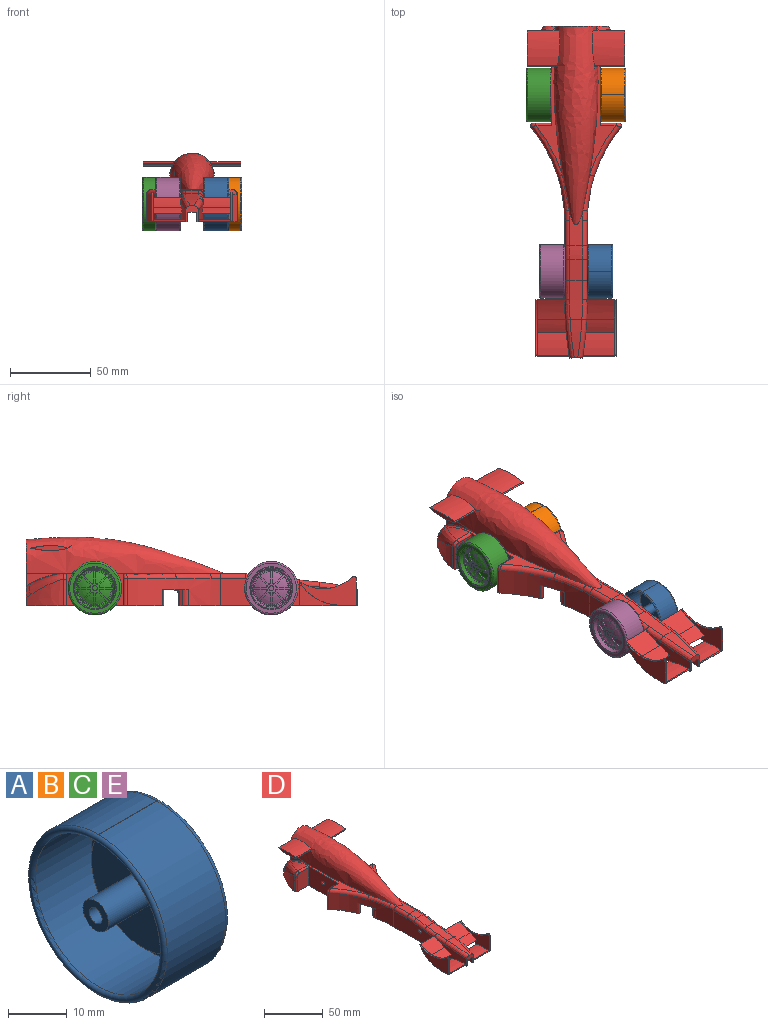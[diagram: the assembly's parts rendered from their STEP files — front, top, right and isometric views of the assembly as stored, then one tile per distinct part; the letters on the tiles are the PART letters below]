
ASSEMBLY  parts=5 mates=4
PART A: 90 faces, bbox 16.1x36.1x36.1 mm
  f0: cylinder r=16.5mm len=16.5mm, axis (1,0,0), area 362.7mm2, adj f1,f3,f86,f88
  f1: torus R=15.5mm, axis (1,0,0), area 159.3mm2, adj f0,f2,f7,f84,f85,f86,f87,f88
  f2: cylinder r=16.5mm len=33mm, axis (1,0,0), area 1088.4mm2, adj f1,f3,f84,f87
  f3: torus R=15.81mm, axis (1,0,0), area 215.3mm2, adj f0,f2,f8,f84,f85,f86,f87,f88
  f4: torus R=13.24mm, axis (1,0,0), area 10.3mm2, adj f7,f15
  f5: cylinder r=1.55mm len=13mm, axis (1,0,0), area 126.6mm2, adj f6,f13
  f6: cone r=1.55mm half-angle=51.1deg, axis (-1,0,0), area 9.7mm2, adj f5
  f7: plane 31x31mm, normal (1,0,0), area 203.7mm2, adj f1,f4
  f8: cylinder r=15.12mm len=30.24mm, axis (1,0,0), area 1282.5mm2, adj f3,f9
  f9: plane 30.24x30.24mm, normal (-1,0,0), area 177.4mm2, adj f8,f10
  f10: cone r=13.12mm half-angle=16.7deg, axis (1,0,0), area 249.3mm2, adj f9,f11
  f11: plane 24.44x24.44mm, normal (-1,0,0), area 439.9mm2, adj f10,f12
  f12: cylinder r=3.05mm len=11.19mm, axis (1,0,0), area 214.4mm2, adj f11,f13
  f13: plane 6.1x6.1mm, normal (-1,0,0), area 21.7mm2, adj f5,f12
  f14: plane 26.24x26.24mm, normal (1,0,0), area 49.9mm2, adj f15,f17
  f15: cylinder r=13.12mm len=26.24mm, axis (1,0,0), area 0.6mm2, adj f4,f14
  f16: plane 3x3mm, normal (1,0,0), area 7.1mm2, adj f61
  f17: cone r=12.5mm half-angle=16.7deg, axis (1,0,0), area 188.9mm2, adj f14,f18
  f18: torus R=11.31mm, axis (1,0,0), area 65.6mm2, adj f17,f24,f30,f36,f42,f48,f54,f60
  f19: cylinder r=0.75mm len=1.28mm, axis (1,0,0), area 1.3mm2, adj f20,f23,f61,f68
  f20: plane 7.03x3.12mm, normal (0,-1,0), area 4.9mm2, adj f19,f21,f61,f68
  f21: cylinder r=1mm len=1.16mm, axis (1,0,0), area 1.1mm2, adj f20,f24,f61,f68,f69
  f22: cylinder r=1mm len=1.52mm, axis (1,0,0), area 1.1mm2, adj f23,f24,f61,f68,f69
  f23: plane 5.1x5.1mm, normal (0,0.71,-0.71), area 4.9mm2, adj f19,f22,f61,f68
  f24: cylinder r=11.05mm len=4.66mm, axis (1,0,0), area 1.8mm2, adj f18,f21,f22,f69
  f25: cylinder r=1mm len=1.16mm, axis (1,0,0), area 1.1mm2, adj f26,f30,f61,f70,f71
  f26: plane 7.03x3.12mm, normal (0,0,-1), area 4.9mm2, adj f25,f27,f61,f71
  f27: cylinder r=0.75mm len=1.28mm, axis (1,0,0), area 1.3mm2, adj f26,f29,f61,f71
  f28: cylinder r=1mm len=1.52mm, axis (1,0,0), area 1.1mm2, adj f29,f30,f61,f70,f71
  f29: plane 5.1x5.1mm, normal (0,-0.71,0.71), area 4.9mm2, adj f27,f28,f61,f71
  f30: cylinder r=11.05mm len=4.66mm, axis (1,0,0), area 1.8mm2, adj f18,f25,f28,f70
  f31: plane 7.03x3.12mm, normal (0,0,1), area 4.9mm2, adj f32,f35,f61,f72
  f32: cylinder r=1mm len=1.16mm, axis (1,0,0), area 1.1mm2, adj f31,f36,f61,f72,f73
  f33: cylinder r=1mm len=1.52mm, axis (1,0,0), area 1.1mm2, adj f34,f36,f61,f72,f73
  f34: plane 5.1x5.1mm, normal (0,-0.71,-0.71), area 4.9mm2, adj f33,f35,f61,f72
  f35: cylinder r=0.75mm len=1.28mm, axis (1,0,0), area 1.3mm2, adj f31,f34,f61,f72
  f36: cylinder r=11.05mm len=4.66mm, axis (1,0,0), area 1.8mm2, adj f18,f32,f33,f73
  f37: plane 5.1x5.1mm, normal (0,0.71,0.71), area 4.9mm2, adj f38,f41,f61,f80
  f38: cylinder r=1mm len=1.52mm, axis (1,0,0), area 1.1mm2, adj f37,f42,f61,f80,f81
  f39: cylinder r=1mm len=1.16mm, axis (1,0,0), area 1.1mm2, adj f40,f42,f61,f80,f81
  f40: plane 7.03x3.12mm, normal (0,-1,0), area 4.9mm2, adj f39,f41,f61,f80
  f41: cylinder r=0.75mm len=1.28mm, axis (1,0,0), area 1.3mm2, adj f37,f40,f61,f80
  f42: cylinder r=11.05mm len=4.66mm, axis (1,0,0), area 1.8mm2, adj f18,f38,f39,f81
  f43: plane 7.03x3.12mm, normal (0,1,0), area 4.9mm2, adj f44,f47,f61,f74
  f44: cylinder r=1mm len=1.16mm, axis (1,0,0), area 1.1mm2, adj f43,f48,f61,f74,f75
  f45: cylinder r=1mm len=1.52mm, axis (1,0,0), area 1.1mm2, adj f46,f48,f61,f74,f75
  f46: plane 5.1x5.1mm, normal (0,-0.71,0.71), area 4.9mm2, adj f45,f47,f61,f74
  f47: cylinder r=0.75mm len=1.28mm, axis (1,0,0), area 1.3mm2, adj f43,f46,f61,f74
  f48: cylinder r=11.05mm len=4.66mm, axis (1,0,0), area 1.8mm2, adj f18,f44,f45,f75
  f49: plane 5.1x5.1mm, normal (0,0.71,-0.71), area 4.9mm2, adj f50,f53,f61,f76
  f50: cylinder r=1mm len=1.52mm, axis (1,0,0), area 1.1mm2, adj f49,f54,f61,f76,f77
  f51: cylinder r=1mm len=1.16mm, axis (1,0,0), area 1.1mm2, adj f52,f54,f61,f76,f77
  f52: plane 7.03x3.12mm, normal (0,0,1), area 4.9mm2, adj f51,f53,f61,f76
  f53: cylinder r=0.75mm len=1.28mm, axis (1,0,0), area 1.3mm2, adj f49,f52,f61,f76
  f54: cylinder r=11.05mm len=4.66mm, axis (1,0,0), area 1.8mm2, adj f18,f50,f51,f77
  f55: plane 7.03x3.12mm, normal (0,0,-1), area 4.9mm2, adj f56,f59,f61,f78
  f56: cylinder r=1mm len=1.16mm, axis (1,0,0), area 1.1mm2, adj f55,f60,f61,f78,f79
  f57: cylinder r=1mm len=1.52mm, axis (1,0,0), area 1.1mm2, adj f58,f60,f61,f78,f79
  f58: plane 5.1x5.1mm, normal (0,0.71,0.71), area 4.9mm2, adj f57,f59,f61,f78
  f59: cylinder r=0.75mm len=1.28mm, axis (1,0,0), area 1.3mm2, adj f55,f58,f61,f78
  f60: cylinder r=11.05mm len=4.66mm, axis (1,0,0), area 1.8mm2, adj f18,f56,f57,f79
  f61: torus R=1.5mm, axis (1,0,0), area 131.6mm2, adj f16,f18,f19,f20,f21,f22,f23,f25
  f62: plane 5.1x5.1mm, normal (0,-0.71,-0.71), area 4.9mm2, adj f61,f63,f66,f82
  f63: cylinder r=1mm len=1.52mm, axis (1,0,0), area 1.1mm2, adj f61,f62,f67,f82,f83
  f64: cylinder r=1mm len=1.16mm, axis (1,0,0), area 1.1mm2, adj f61,f65,f67,f82,f83
  f65: plane 7.03x3.12mm, normal (0,1,0), area 4.9mm2, adj f61,f64,f66,f82
  f66: cylinder r=0.75mm len=1.28mm, axis (1,0,0), area 1.3mm2, adj f61,f62,f65,f82
  f67: cylinder r=11.05mm len=4.66mm, axis (1,0,0), area 1.8mm2, adj f18,f63,f64,f83
  f68: torus R=1.5mm, axis (1,0,0), area 29.3mm2, adj f19,f20,f21,f22,f23,f69
  f69: plane 6.16x3.12mm, normal (1,0,0), area 4.5mm2, adj f21,f22,f24,f68
  f70: plane 6.16x3.12mm, normal (1,0,0), area 4.5mm2, adj f25,f28,f30,f71
  f71: torus R=1.5mm, axis (1,0,0), area 29.3mm2, adj f25,f26,f27,f28,f29,f70
  f72: torus R=1.5mm, axis (1,0,0), area 29.3mm2, adj f31,f32,f33,f34,f35,f73
  f73: plane 6.16x3.12mm, normal (1,0,0), area 4.5mm2, adj f32,f33,f36,f72
  f74: torus R=1.5mm, axis (1,0,0), area 29.3mm2, adj f43,f44,f45,f46,f47,f75
  f75: plane 6.16x3.12mm, normal (1,0,0), area 4.5mm2, adj f44,f45,f48,f74
  f76: torus R=1.5mm, axis (1,0,0), area 29.3mm2, adj f49,f50,f51,f52,f53,f77
  f77: plane 6.16x3.12mm, normal (1,0,0), area 4.5mm2, adj f50,f51,f54,f76
  f78: torus R=1.5mm, axis (1,0,0), area 29.3mm2, adj f55,f56,f57,f58,f59,f79
  f79: plane 6.16x3.12mm, normal (1,0,0), area 4.5mm2, adj f56,f57,f60,f78
  f80: torus R=1.5mm, axis (1,0,0), area 29.3mm2, adj f37,f38,f39,f40,f41,f81
  f81: plane 6.16x3.12mm, normal (1,0,0), area 4.5mm2, adj f38,f39,f42,f80
  f82: torus R=1.5mm, axis (1,0,0), area 29.3mm2, adj f62,f63,f64,f65,f66,f83
  f83: plane 6.16x3.12mm, normal (1,0,0), area 4.5mm2, adj f63,f64,f67,f82
  f84: plane 14.18x0.01mm, normal (0,1,0), area 0.1mm2, adj f1,f2,f3,f85
  f85: plane 14.18x0.01mm, normal (0,0,1), area 0.1mm2, adj f1,f3,f84,f86
  f86: plane 14.18x0.01mm, normal (0,-1,0), area 0.1mm2, adj f0,f1,f3,f85
  f87: plane 14.18x0.01mm, normal (0,0,1), area 0.1mm2, adj f1,f2,f3,f89
  f88: plane 14.18x0.01mm, normal (0,0,-1), area 0.1mm2, adj f0,f1,f3,f89
  f89: plane 14.18x0.01mm, normal (0,1,0), area 0.1mm2, adj f1,f3,f87,f88
PART B: same geometry as A
PART C: same geometry as A
PART D: 160 faces, bbox 60.7x214.2x51 mm
  f0: plane 66.79x20.53mm, normal (0,0,1), area 391.4mm2, adj f3,f6,f43,f49,f107,f116,f120,f143
  f1: plane 66.78x20.53mm, normal (0,0,1), area 391.4mm2, adj f2,f5,f6,f42,f47,f116,f129,f140
  f2: bspline ~135x17.28mm, area 183.9mm2, adj f1,f5,f6,f116
  f3: bspline ~135x17.28mm, area 183.9mm2, adj f0,f6,f107,f116
  f4: plane 21.67x8.38mm, normal (0,0,1), area 126mm2, adj f6,f22,f122,f123,f131,f132
  f5: plane 9.31x0.16mm, normal (0,-1,0), area 1.5mm2, adj f1,f2,f106,f116
  f6: bspline ~122.68x27.34mm, area 5446.4mm2, adj f0,f1,f2,f3,f4,f7,f105,f106
  f7: plane 41.59x40.59mm, normal (0,1,0), area 629.2mm2, adj f6,f32,f36,f41,f45,f50,f55,f57
  f8: extruded ~24.99x7.5mm, area 9.7mm2, adj f49,f55,f105
  f9: extruded ~24.99x7.5mm, area 11.3mm2, adj f47,f57,f106
  f10: cylinder r=53.29mm len=20.77mm, axis (-1,0,0), area 290.9mm2, adj f11,f12,f17,f96,f98
  f11: cylinder r=53.29mm len=19.77mm, axis (-1,0,0), area 276.2mm2, adj f10,f12,f17,f99
  f12: cylinder r=0.45mm len=20.77mm, axis (-1,0,0), area 26.6mm2, adj f10,f11,f17,f97,f98,f99
  f13: cylinder r=62.23mm len=17.75mm, axis (-1,0,0), area 232.9mm2, adj f14,f16,f17,f99,f136
  f14: cylinder r=50mm len=17.93mm, axis (-1,0,0), area 157mm2, adj f13,f15,f17,f99
  f15: plane 17.93x2.95mm, normal (0,0.17,-0.98), area 53.4mm2, adj f14,f16,f17,f99
  f16: cylinder r=29.92mm len=17.75mm, axis (-1,0,0), area 344.5mm2, adj f13,f15,f17,f99,f136
  f17: cylinder r=220.68mm len=36.26mm, axis (0,0,1), area 336.4mm2, adj f10,f11,f12,f13,f14,f15,f16,f27
  f18: cylinder r=220.68mm len=36.26mm, axis (0,0,1), area 336.4mm2, adj f20,f27,f86,f88,f89,f90,f91,f92
  f19: plane 72.73x29.07mm, normal (0,0,-1), area 836.9mm2, adj f25,f26,f32,f34,f35,f61,f69,f70
  f20: plane 110.7x6.33mm, normal (0,0,-1), area 239.3mm2, adj f18,f25,f27,f28,f82,f85,f86,f148
  f21: plane 12.97x8mm, normal (0,-0.14,0.99), area 104.8mm2, adj f22,f24,f125,f134
  f22: cylinder r=60mm len=8.49mm, axis (1,0,0), area 68.1mm2, adj f4,f21,f124,f133
  f23: bspline ~30x30mm, area 118.3mm2, adj f24,f27,f128,f137
  f24: bspline ~24.13x11.17mm, area 190.1mm2, adj f21,f23,f126,f127,f135,f136
  f25: plane 10x6.68mm, normal (0.87,0.48,0), area 20.6mm2, adj f19,f20,f76,f146,f147,f148,f158
  f26: cylinder r=30mm len=10mm, axis (0,0,-1), area 84.3mm2, adj f19,f41,f69,f144
  f27: plane 10.49x8.49mm, normal (0,-1,0), area 40.4mm2, adj f17,f18,f20,f23,f44,f82,f128,f137
  f28: plane 69.2x7.24mm, normal (-1,0,0), area 466.2mm2, adj f20,f34,f38,f64,f82,f148
  f29: plane 69.2x7.25mm, normal (1,0,0), area 466.2mm2, adj f35,f39,f44,f65,f82,f149
  f30: plane 21x1.69mm, normal (0,0,-1), area 35.4mm2, adj f31,f33,f37,f71
  f31: plane 5.87x2.1mm, normal (-1,0,0), area 8mm2, adj f30,f37,f40,f71
  f32: plane 75.59x10mm, normal (1,0,0), area 697.4mm2, adj f7,f19,f36,f59,f72,f73,f74,f75
  f33: plane 5.87x2.1mm, normal (1,0,0), area 8mm2, adj f30,f37,f40,f71
  f34: extruded ~48.21x2.99mm, area 170.3mm2, adj f19,f28,f62,f80,f81,f147
  f35: extruded ~48.21x2.99mm, area 170.3mm2, adj f19,f29,f63,f78,f79,f150
  f36: plane 85.05x19.56mm, normal (0,0,-1), area 808mm2, adj f7,f32,f42,f45,f48,f54,f73,f83
  f37: cylinder r=1.6mm len=30mm, axis (-1,0,0), area 241.4mm2, adj f30,f31,f33,f40,f42,f43
  f38: extruded ~0.48x0.41mm, area 0.1mm2, adj f28,f66,f82
  f39: extruded ~0.48x0.41mm, area 0.1mm2, adj f29,f67,f82
  f40: plane 21x1.69mm, normal (0,0,-1), area 35.4mm2, adj f31,f33,f37,f71
  f41: plane 85.05x19.56mm, normal (0,0,-1), area 808mm2, adj f7,f26,f43,f50,f52,f53,f69,f85
  f42: plane 38.14x20.05mm, normal (-1,0,0), area 693mm2, adj f1,f36,f37,f47,f48,f54,f140,f153
  f43: plane 38.14x20.05mm, normal (1,0,0), area 693mm2, adj f0,f37,f41,f49,f52,f53,f143,f155
  f44: plane 110.7x6.33mm, normal (0,0,-1), area 238.4mm2, adj f17,f27,f29,f70,f82,f83,f84,f149
  f45: bspline ~25x20mm, area 284mm2, adj f7,f36,f57,f58,f152
  f46: bspline ~25x15mm, area 104.7mm2, adj f47,f58,f153
  f47: extruded ~24.39x7.22mm, area 46.3mm2, adj f1,f9,f42,f46,f57
  f48: plane 18.46x13.45mm, normal (0,-1,0), area 247.4mm2, adj f36,f42,f152,f153,f154
  f49: extruded ~24.4x7.23mm, area 46.4mm2, adj f0,f8,f43,f51,f55
  f50: bspline ~25x20mm, area 284mm2, adj f7,f41,f55,f56,f156
  f51: bspline ~25x15mm, area 104.7mm2, adj f49,f56,f155
  f52: plane 18.46x13.44mm, normal (0,-1,0), area 247.4mm2, adj f41,f43,f155,f156,f157
  f53: plane 18.5x11.72mm, normal (0,1,0), area 216.1mm2, adj f41,f43,f141,f142,f143
  f54: plane 18.5x11.72mm, normal (0,1,0), area 216.1mm2, adj f36,f42,f138,f139,f140
  f55: bspline ~9.3x9.24mm, area 37.1mm2, adj f7,f8,f49,f50,f56
  f56: bspline ~27.26x18.15mm, area 196.7mm2, adj f50,f51,f55,f157
  f57: bspline ~9.3x9.24mm, area 37mm2, adj f7,f9,f45,f47,f58
  f58: bspline ~27.26x18.15mm, area 196.7mm2, adj f45,f46,f57,f154
  f59: plane 21.44x21mm, normal (0,0,-1), area 450.3mm2, adj f7,f32,f69,f74
  f60: cylinder r=41.85mm len=29.2mm, axis (-1,0,0), area 174.6mm2, adj f61,f62,f63,f64,f65,f66,f67,f68
  f61: cylinder r=2mm len=4.02mm, axis (-1,0,0), area 2.9mm2, adj f19,f60,f62,f63
  f62: bspline ~3.98x2.89mm, area 6.3mm2, adj f34,f60,f61,f64
  f63: bspline ~3.98x2.9mm, area 6.3mm2, adj f35,f60,f61,f65
  f64: torus R=43.85mm, axis (1,0,0), area 81.1mm2, adj f28,f60,f62,f66
  f65: torus R=43.85mm, axis (-1,0,0), area 81.1mm2, adj f29,f60,f63,f67
  f66: bspline ~3.98x2.89mm, area 5.8mm2, adj f38,f60,f64,f68,f82
  f67: bspline ~3.98x2.9mm, area 5.8mm2, adj f39,f60,f65,f68,f82
  f68: cylinder r=2mm len=4.02mm, axis (-1,0,0), area 2.1mm2, adj f60,f66,f67,f82
  f69: plane 75.59x10mm, normal (-1,0,0), area 697.4mm2, adj f7,f19,f26,f41,f59,f72,f74,f75
  f70: plane 10x6.68mm, normal (-0.87,0.48,0), area 20.6mm2, adj f19,f44,f77,f149,f150,f151,f159
  f71: cylinder r=3.1mm len=21mm, axis (-1,0,0), area 161.8mm2, adj f30,f31,f33,f40
  f72: cylinder r=41.85mm len=21.53mm, axis (-1,0,0), area 457.4mm2, adj f32,f69,f74,f75
  f73: cylinder r=30mm len=10mm, axis (0,0,-1), area 84.3mm2, adj f19,f32,f36,f145
  f74: cylinder r=40mm len=21mm, axis (-1,0,0), area 218.6mm2, adj f32,f59,f69,f72
  f75: cylinder r=40mm len=21mm, axis (-1,0,0), area 218.6mm2, adj f19,f32,f69,f72
  f76: plane 4.81x4.68mm, normal (0,0.08,-1), area 9.1mm2, adj f19,f25,f81,f146
  f77: plane 4.81x4.68mm, normal (0,0.08,-1), area 9.1mm2, adj f19,f70,f78,f151
  f78: bspline ~27.44x5.62mm, area 18.2mm2, adj f19,f35,f77,f79,f151
  f79: bspline ~25.87x5.18mm, area 12mm2, adj f35,f78,f151
  f80: bspline ~24.87x5.11mm, area 12mm2, adj f34,f81,f146
  f81: bspline ~32.15x6.03mm, area 18.2mm2, adj f19,f34,f76,f80,f146
  f82: bspline ~40x10mm, area 943.8mm2, adj f20,f27,f28,f29,f38,f39,f44,f66
  f83: cylinder r=89.76mm len=57.54mm, axis (0,0,1), area 891.9mm2, adj f19,f36,f44,f84,f129,f130,f131,f138
  f84: plane 48.74x17mm, normal (-1,0,0), area 760.8mm2, adj f17,f44,f83,f87,f132,f133,f134,f135
  f85: cylinder r=89.76mm len=57.54mm, axis (0,0,1), area 891.9mm2, adj f19,f20,f41,f86,f120,f121,f122,f141
  f86: plane 48.74x17mm, normal (1,0,0), area 760.8mm2, adj f18,f20,f85,f87,f123,f124,f125,f126
  f87: cylinder r=1.6mm len=14mm, axis (-1,0,0), area 140.7mm2, adj f84,f86
  f88: cylinder r=53.29mm len=19.77mm, axis (1,0,0), area 276.2mm2, adj f18,f89,f90,f100
  f89: cylinder r=53.29mm len=20.77mm, axis (1,0,0), area 290.9mm2, adj f18,f88,f90,f101,f104
  f90: cylinder r=0.45mm len=20.77mm, axis (1,0,0), area 26.6mm2, adj f18,f88,f89,f100,f103,f104
  f91: cylinder r=29.92mm len=17.75mm, axis (1,0,0), area 344.5mm2, adj f18,f92,f94,f100,f127
  f92: plane 17.93x2.95mm, normal (0,0.17,-0.98), area 53.4mm2, adj f18,f91,f93,f100
  f93: cylinder r=50mm len=17.93mm, axis (1,0,0), area 157mm2, adj f18,f92,f94,f100
  f94: cylinder r=62.23mm len=17.75mm, axis (1,0,0), area 232.9mm2, adj f18,f91,f93,f100,f127
  f95: cylinder r=26.41mm len=32.48mm, axis (1,0,0), area 35.1mm2, adj f96,f98,f99,f119
  f96: cylinder r=28.53mm len=20mm, axis (1,0,0), area 25.2mm2, adj f10,f95,f98,f99
  f97: plane 15.69x1mm, normal (0,-1,0), area 15.7mm2, adj f12,f98,f99,f119
  f98: plane 35x17.94mm, normal (-1,0,0), area 330.6mm2, adj f10,f12,f95,f96,f97,f119
  f99: plane 35x17.19mm, normal (1,0,0), area 286.5mm2, adj f11,f12,f13,f14,f15,f16,f95,f96
  f100: plane 35x17.19mm, normal (-1,0,0), area 286.5mm2, adj f88,f90,f91,f92,f93,f94,f101,f102
  f101: cylinder r=28.53mm len=20mm, axis (-1,0,0), area 25.2mm2, adj f89,f100,f102,f104
  f102: cylinder r=26.41mm len=32.48mm, axis (-1,0,0), area 35.1mm2, adj f100,f101,f104,f118
  f103: plane 15.69x1mm, normal (0,-1,0), area 15.7mm2, adj f90,f100,f104,f118
  f104: plane 35x17.94mm, normal (1,0,0), area 330.6mm2, adj f89,f90,f101,f102,f103,f118
  f105: extruded ~25x7.66mm, area 62.8mm2, adj f6,f7,f8,f107
  f106: extruded ~25x7.66mm, area 62.8mm2, adj f5,f6,f7,f9
  f107: plane 9.31x0.16mm, normal (0,-1,0), area 1.5mm2, adj f0,f3,f105,f116
  f108: plane 22x3mm, normal (-1,0,0), area 46.8mm2, adj f109,f110,f111
  f109: cylinder r=47.74mm len=21.59mm, axis (1,0,0), area 409.7mm2, adj f6,f108,f110,f111
  f110: cylinder r=47.74mm len=21.59mm, axis (1,0,0), area 416mm2, adj f6,f108,f109,f111
  f111: cylinder r=0.51mm len=18.61mm, axis (1,0,0), area 25.6mm2, adj f6,f108,f109,f110
  f112: cylinder r=0.51mm len=18.61mm, axis (1,0,0), area 25.6mm2, adj f6,f113,f114,f115
  f113: cylinder r=47.74mm len=21.59mm, axis (1,0,0), area 409.7mm2, adj f6,f112,f114,f115
  f114: plane 22x3mm, normal (1,0,0), area 46.8mm2, adj f112,f113,f115
  f115: cylinder r=47.74mm len=21.59mm, axis (1,0,0), area 416mm2, adj f6,f112,f113,f114
  f116: cylinder r=9.5mm len=52mm, axis (0,1,0), area 3094.2mm2, adj f0,f1,f2,f3,f5,f7,f107,f117
  f117: plane 19x19mm, normal (0,1,0), area 283.5mm2, adj f116
  f118: cylinder r=1.5mm len=2.52mm, axis (-1,0,0), area 3.5mm2, adj f100,f102,f103,f104
  f119: cylinder r=1.5mm len=2.52mm, axis (1,0,0), area 3.5mm2, adj f95,f97,f98,f99
  f120: torus R=92.76mm, axis (0,0,1), area 162.7mm2, adj f0,f85,f121,f142
  f121: bspline ~24.86x7.76mm, area 92.2mm2, adj f6,f85,f120,f122
  f122: torus R=92.76mm, axis (0,0,1), area 27.4mm2, adj f4,f85,f121,f123
  f123: cylinder r=3mm len=15.74mm, axis (0,1,0), area 74.2mm2, adj f4,f86,f122,f124
  f124: torus R=57mm, axis (-1,0,0), area 39.4mm2, adj f22,f86,f123,f125
  f125: cylinder r=3mm len=13.4mm, axis (0,0.99,0.14), area 61.8mm2, adj f21,f86,f124,f126
  f126: bspline ~60.05x10.76mm, area 56.7mm2, adj f24,f86,f125,f127
  f127: bspline ~28.38x5.67mm, area 56.6mm2, adj f18,f24,f91,f94,f126,f128
  f128: bspline ~31.75x9.02mm, area 113.6mm2, adj f18,f23,f27,f127
  f129: torus R=92.76mm, axis (0,0,1), area 162.7mm2, adj f1,f83,f130,f139
  f130: bspline ~24.32x7.57mm, area 92.2mm2, adj f6,f83,f129,f131
  f131: torus R=92.76mm, axis (0,0,1), area 27.4mm2, adj f4,f83,f130,f132
  f132: cylinder r=3mm len=15.74mm, axis (0,-1,0), area 74.2mm2, adj f4,f84,f131,f133
  f133: torus R=57mm, axis (-1,0,0), area 39.4mm2, adj f22,f84,f132,f134
  f134: cylinder r=3mm len=13.4mm, axis (0,-0.99,-0.14), area 61.7mm2, adj f21,f84,f133,f135
  f135: bspline ~60.05x10.76mm, area 56.7mm2, adj f24,f84,f134,f136
  f136: bspline ~37.77x6.92mm, area 56.6mm2, adj f13,f16,f17,f24,f135,f137
  f137: bspline ~31.75x9.02mm, area 113.6mm2, adj f17,f23,f27,f136
  f138: cylinder r=1.5mm len=17mm, axis (0,0,1), area 57.8mm2, adj f36,f54,f83,f139
  f139: bspline ~5.96x4.27mm, area 13.2mm2, adj f54,f129,f138,f140
  f140: cylinder r=1.5mm len=9.77mm, axis (1,0,0), area 23mm2, adj f1,f42,f54,f139
  f141: cylinder r=1.5mm len=17mm, axis (0,0,1), area 57.8mm2, adj f41,f53,f85,f142
  f142: bspline ~5.96x4.27mm, area 13.2mm2, adj f53,f120,f141,f143
  f143: cylinder r=1.5mm len=9.77mm, axis (1,0,0), area 23mm2, adj f0,f43,f53,f142
  f144: cylinder r=1.5mm len=10mm, axis (0,0,-1), area 36.7mm2, adj f19,f26,f41,f85
  f145: cylinder r=1.5mm len=10mm, axis (0,0,-1), area 36.7mm2, adj f19,f36,f73,f83
  f146: bspline ~5.81x5.31mm, area 6.8mm2, adj f25,f76,f80,f81,f147
  f147: bspline ~5.8x3.44mm, area 3.6mm2, adj f25,f34,f146,f148
  f148: cylinder r=1.5mm len=7.24mm, axis (0,0,1), area 28.6mm2, adj f20,f25,f28,f147
  f149: cylinder r=1.5mm len=7.24mm, axis (0,0,1), area 28.6mm2, adj f29,f44,f70,f150
  f150: bspline ~5.8x3.44mm, area 3.6mm2, adj f35,f70,f149,f151
  f151: bspline ~5.64x5.58mm, area 6.8mm2, adj f70,f77,f78,f79,f150
  f152: bspline ~27.85x1.62mm, area 41mm2, adj f36,f45,f48,f154
  f153: bspline ~16.46x1.58mm, area 28.3mm2, adj f42,f46,f48,f154
  f154: bspline ~3.33x3.32mm, area 11.4mm2, adj f48,f58,f152,f153
  f155: bspline ~16.46x1.58mm, area 28.3mm2, adj f43,f51,f52,f157
  f156: bspline ~27.87x1.62mm, area 41mm2, adj f41,f50,f52,f157
  f157: bspline ~3.52x3.51mm, area 11.4mm2, adj f52,f56,f155,f156
  f158: cylinder r=5mm len=10mm, axis (0,0,1), area 36.4mm2, adj f19,f20,f25,f85
  f159: cylinder r=5mm len=10mm, axis (0,0,1), area 36.4mm2, adj f19,f44,f70,f83
PART E: same geometry as A
PLACE A t=(-10.71,-100.56,-57.32)mm
PLACE B t=(-2.71,8.44,-57.32)mm
PLACE C rot(axis=(0,1,0),180deg) t=(-64.09,8.44,-57.32)mm
PLACE D t=(-33.4,50.94,-39.82)mm
PLACE E rot(axis=(0,1,0),180deg) t=(-56.09,-100.56,-57.32)mm
MATE revolute A.f0 <-> D.f87  axis (-1,0,0) through (-26.4,-100.56,-57.32)mm
MATE revolute E.f0 <-> D.f87  axis (1,0,0) through (-40.4,-100.56,-57.32)mm
MATE revolute B.f0 <-> D.f37  axis (-1,0,0) through (-18.4,8.44,-57.32)mm
MATE revolute C.f0 <-> D.f37  axis (1,0,0) through (-48.4,8.44,-57.32)mm
